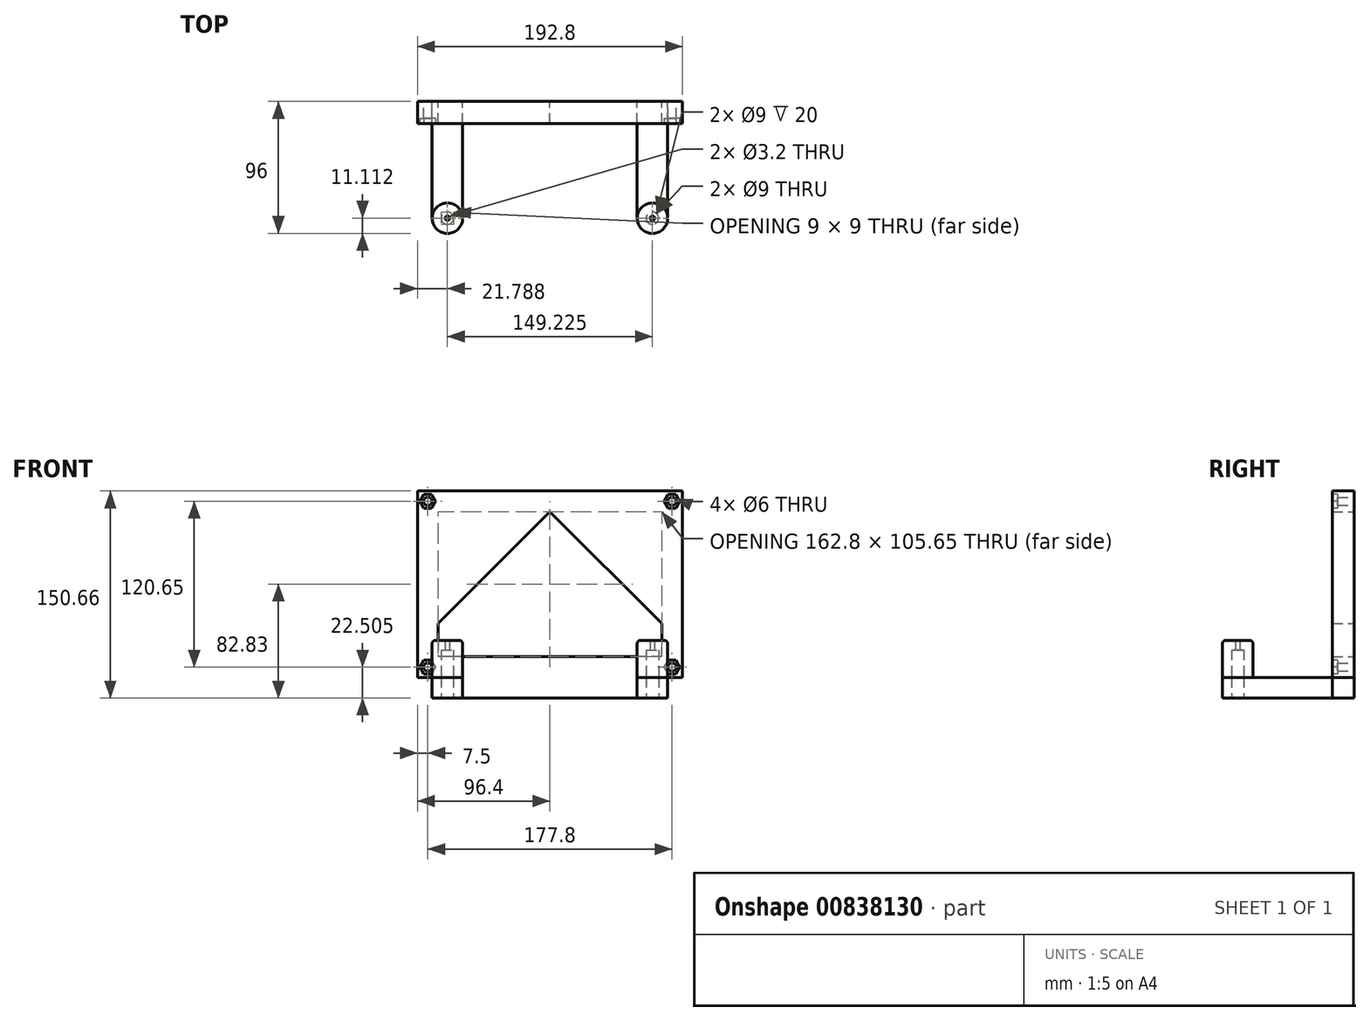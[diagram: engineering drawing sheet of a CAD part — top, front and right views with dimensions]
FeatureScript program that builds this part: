
annotation { "Feature Type Name" : "Feature", "Feature Type Description" : "" }
export const myFeature = defineFeature(function(context is Context, id is Id, definition is map)
    precondition{}
    {
        {
            var Q0;
            Q0=qCreatedBy(makeId("Front.planeOp"),FACE);
            var sketch = newSketch(context, id + "F0", { "sketchPlane" : qUnion([Q0])});
            skLineSegment(sketch, "E0.bottom", {"start": v(-88.9, 60.33) * mm, "end": v(88.9, 60.33) * mm, "construction": true});
            skLineSegment(sketch, "E0.top", {"start": v(-88.9, -60.32) * mm, "end": v(88.9, -60.32) * mm, "construction": true});
            skLineSegment(sketch, "E0.left", {"start": v(-88.9, 60.33) * mm, "end": v(-88.9, -60.32) * mm, "construction": true});
            skLineSegment(sketch, "E0.right", {"start": v(88.9, 60.33) * mm, "end": v(88.9, -60.32) * mm, "construction": true});
            skPoint(sketch, "E0.middle", {"position": v(0, 0) * mm});
            skCircle(sketch, "E1", {"center": v(-88.9, 60.33) * mm, "radius": 3 * mm});
            skCircle(sketch, "E2", {"center": v(88.9, 60.33) * mm, "radius": 3 * mm});
            skCircle(sketch, "E3", {"center": v(88.9, -60.32) * mm, "radius": 3 * mm});
            skCircle(sketch, "E4", {"center": v(-88.9, -60.32) * mm, "radius": 3 * mm});
            skLineSegment(sketch, "E5.bottom", {"start": v(-88.9, 60.33) * mm, "end": v(-96.4, 60.33) * mm, "construction": true});
            skLineSegment(sketch, "E5.top", {"start": v(-88.9, 67.83) * mm, "end": v(-96.4, 67.83) * mm, "construction": true});
            skLineSegment(sketch, "E5.left", {"start": v(-88.9, 60.33) * mm, "end": v(-88.9, 67.83) * mm, "construction": true});
            skLineSegment(sketch, "E5.right", {"start": v(-96.4, 60.33) * mm, "end": v(-96.4, 67.83) * mm, "construction": true});
            skLineSegment(sketch, "E6.bottom", {"start": v(88.9, -60.32) * mm, "end": v(96.4, -60.32) * mm, "construction": true});
            skLineSegment(sketch, "E6.top", {"start": v(88.9, -67.83) * mm, "end": v(96.4, -67.83) * mm, "construction": true});
            skLineSegment(sketch, "E6.left", {"start": v(88.9, -60.32) * mm, "end": v(88.9, -67.83) * mm, "construction": true});
            skLineSegment(sketch, "E6.right", {"start": v(96.4, -60.32) * mm, "end": v(96.4, -67.83) * mm, "construction": true});
            skLineSegment(sketch, "E7.bottom", {"start": v(-96.4, 67.83) * mm, "end": v(-81.4, 67.83) * mm});
            skLineSegment(sketch, "E7.top", {"start": v(-96.4, -67.83) * mm, "end": v(-81.4, -67.83) * mm});
            skLineSegment(sketch, "E7.left", {"start": v(-96.4, 67.83) * mm, "end": v(-96.4, -67.83) * mm});
            skLineSegment(sketch, "E7.right", {"start": v(-81.4, 67.83) * mm, "end": v(-81.4, -67.83) * mm});
            skLineSegment(sketch, "E8.bottom", {"start": v(96.4, -67.83) * mm, "end": v(-96.4, -67.83) * mm});
            skLineSegment(sketch, "E8.top", {"start": v(96.4, -52.82) * mm, "end": v(-96.4, -52.83) * mm});
            skLineSegment(sketch, "E8.left", {"start": v(96.4, -67.83) * mm, "end": v(96.4, -52.82) * mm});
            skLineSegment(sketch, "E8.right", {"start": v(-96.4, -67.83) * mm, "end": v(-96.4, -52.83) * mm});
            skLineSegment(sketch, "E9.bottom", {"start": v(96.4, -67.83) * mm, "end": v(81.4, -67.83) * mm});
            skLineSegment(sketch, "E9.top", {"start": v(96.4, 67.83) * mm, "end": v(81.4, 67.83) * mm});
            skLineSegment(sketch, "E9.left", {"start": v(96.4, -67.83) * mm, "end": v(96.4, 67.83) * mm});
            skLineSegment(sketch, "E9.right", {"start": v(81.4, -67.83) * mm, "end": v(81.4, 67.83) * mm});
            skLineSegment(sketch, "E10.bottom", {"start": v(-96.4, 67.83) * mm, "end": v(96.4, 67.83) * mm});
            skLineSegment(sketch, "E10.top", {"start": v(-96.4, 52.83) * mm, "end": v(96.4, 52.83) * mm});
            skLineSegment(sketch, "E10.left", {"start": v(-96.4, 67.83) * mm, "end": v(-96.4, 52.83) * mm});
            skLineSegment(sketch, "E10.right", {"start": v(96.4, 67.83) * mm, "end": v(96.4, 52.83) * mm});
            skLineSegment(sketch, "E11.bottom", {"start": v(0, -67.83) * mm, "end": v(-85.72, -67.83) * mm, "construction": true});
            skLineSegment(sketch, "E11.top", {"start": v(0, -82.83) * mm, "end": v(-85.72, -82.83) * mm, "construction": true});
            skLineSegment(sketch, "E11.left", {"start": v(0, -67.83) * mm, "end": v(0, -82.83) * mm, "construction": true});
            skLineSegment(sketch, "E11.right", {"start": v(-85.72, -67.83) * mm, "end": v(-85.72, -82.83) * mm, "construction": true});
            skLineSegment(sketch, "E12.bottom", {"start": v(0, -67.83) * mm, "end": v(85.73, -67.83) * mm, "construction": true});
            skLineSegment(sketch, "E12.top", {"start": v(0, -82.83) * mm, "end": v(85.73, -82.83) * mm, "construction": true});
            skLineSegment(sketch, "E12.right", {"start": v(85.73, -67.83) * mm, "end": v(85.73, -82.83) * mm, "construction": true});
            skLineSegment(sketch, "E13.bottom", {"start": v(-85.72, -82.83) * mm, "end": v(85.73, -82.83) * mm});
            skLineSegment(sketch, "E13.top", {"start": v(-85.72, -67.83) * mm, "end": v(85.73, -67.83) * mm});
            skLineSegment(sketch, "E13.left", {"start": v(-85.72, -82.83) * mm, "end": v(-85.72, -67.83) * mm});
            skLineSegment(sketch, "E13.right", {"start": v(85.73, -82.83) * mm, "end": v(85.73, -67.83) * mm});
            skLineSegment(sketch, "E14.bottom", {"start": v(85.73, -67.83) * mm, "end": v(70.73, -67.83) * mm});
            skLineSegment(sketch, "E14.left", {"start": v(85.73, -67.83) * mm, "end": v(85.73, -82.83) * mm});
            skLineSegment(sketch, "E15.bottom", {"start": v(-85.72, -67.83) * mm, "end": v(-63.5, -67.83) * mm});
            skLineSegment(sketch, "E15.top", {"start": v(-85.72, -82.83) * mm, "end": v(-63.5, -82.83) * mm});
            skLineSegment(sketch, "E15.left", {"start": v(-85.72, -67.83) * mm, "end": v(-85.72, -82.83) * mm});
            skLineSegment(sketch, "E15.right", {"start": v(-63.5, -67.83) * mm, "end": v(-63.5, -82.83) * mm});
            skLineSegment(sketch, "E16.bottom", {"start": v(85.73, -67.83) * mm, "end": v(63.5, -67.83) * mm});
            skLineSegment(sketch, "E16.top", {"start": v(85.73, -82.83) * mm, "end": v(63.5, -82.83) * mm});
            skLineSegment(sketch, "E16.right", {"start": v(63.5, -67.83) * mm, "end": v(63.5, -82.83) * mm});
            skLineSegment(sketch, "E17", {"start": v(0, 52.83) * mm, "end": v(81.4, -28.57) * mm});
            skLineSegment(sketch, "E18", {"start": v(0, 52.83) * mm, "end": v(-81.4, -28.57) * mm});
            skCircle(sketch, "E19.cCircle", {"center": v(88.9, 60.33) * mm, "radius": 4.95 * mm, "construction": true});
            skLineSegment(sketch, "E19.0", {"start": v(91.76, 55.38) * mm, "end": v(86.04, 55.38) * mm});
            skLineSegment(sketch, "E19.1", {"start": v(86.04, 55.38) * mm, "end": v(83.18, 60.32) * mm});
            skLineSegment(sketch, "E19.2", {"start": v(83.18, 60.32) * mm, "end": v(86.04, 65.28) * mm});
            skLineSegment(sketch, "E19.3", {"start": v(86.04, 65.27) * mm, "end": v(91.76, 65.27) * mm});
            skLineSegment(sketch, "E19.4", {"start": v(91.76, 65.28) * mm, "end": v(94.62, 60.33) * mm});
            skLineSegment(sketch, "E19.5", {"start": v(94.62, 60.33) * mm, "end": v(91.76, 55.38) * mm});
            skPoint(sketch, "E19.0.midPoint", {"position": v(88.9, 55.38) * mm});
            skCircle(sketch, "E20.cCircle", {"center": v(88.9, -60.32) * mm, "radius": 4.95 * mm, "construction": true});
            skLineSegment(sketch, "E20.0", {"start": v(86.04, -55.37) * mm, "end": v(91.76, -55.37) * mm});
            skLineSegment(sketch, "E20.1", {"start": v(91.76, -55.37) * mm, "end": v(94.62, -60.32) * mm});
            skLineSegment(sketch, "E20.2", {"start": v(94.62, -60.32) * mm, "end": v(91.76, -65.28) * mm});
            skLineSegment(sketch, "E20.3", {"start": v(91.76, -65.28) * mm, "end": v(86.04, -65.28) * mm});
            skLineSegment(sketch, "E20.4", {"start": v(86.04, -65.28) * mm, "end": v(83.18, -60.32) * mm});
            skLineSegment(sketch, "E20.5", {"start": v(83.18, -60.32) * mm, "end": v(86.04, -55.37) * mm});
            skPoint(sketch, "E20.0.midPoint", {"position": v(88.9, -55.37) * mm});
            skCircle(sketch, "E21.cCircle", {"center": v(-88.9, -60.32) * mm, "radius": 4.95 * mm, "construction": true});
            skLineSegment(sketch, "E21.0", {"start": v(-91.76, -55.38) * mm, "end": v(-86.04, -55.38) * mm});
            skLineSegment(sketch, "E21.1", {"start": v(-86.04, -55.38) * mm, "end": v(-83.18, -60.33) * mm});
            skLineSegment(sketch, "E21.2", {"start": v(-83.18, -60.33) * mm, "end": v(-86.04, -65.28) * mm});
            skLineSegment(sketch, "E21.3", {"start": v(-86.04, -65.27) * mm, "end": v(-91.76, -65.27) * mm});
            skLineSegment(sketch, "E21.4", {"start": v(-91.76, -65.28) * mm, "end": v(-94.62, -60.33) * mm});
            skLineSegment(sketch, "E21.5", {"start": v(-94.62, -60.33) * mm, "end": v(-91.76, -55.38) * mm});
            skPoint(sketch, "E21.0.midPoint", {"position": v(-88.9, -55.38) * mm});
            skCircle(sketch, "E22.cCircle", {"center": v(-88.9, 60.33) * mm, "radius": 4.95 * mm, "construction": true});
            skLineSegment(sketch, "E22.0", {"start": v(-86.04, 55.38) * mm, "end": v(-91.76, 55.38) * mm});
            skLineSegment(sketch, "E22.1", {"start": v(-91.76, 55.37) * mm, "end": v(-94.62, 60.33) * mm});
            skLineSegment(sketch, "E22.2", {"start": v(-94.62, 60.32) * mm, "end": v(-91.76, 65.28) * mm});
            skLineSegment(sketch, "E22.3", {"start": v(-91.76, 65.28) * mm, "end": v(-86.04, 65.28) * mm});
            skLineSegment(sketch, "E22.4", {"start": v(-86.04, 65.28) * mm, "end": v(-83.18, 60.33) * mm});
            skLineSegment(sketch, "E22.5", {"start": v(-83.18, 60.33) * mm, "end": v(-86.04, 55.38) * mm});
            skPoint(sketch, "E22.0.midPoint", {"position": v(-88.9, 55.38) * mm});
            skSolve(sketch);
        }
        {
            var Q0;
            Q0=makeQuery(id+"F0.imprint","IMPRINT",FACE,{"disambiguationData":[TD([[makeQuery(id+"F0.imprint","IMPRINT",EDGE,{"derivedFrom":sQuery(id+"F0.wireOp",EDGE,"E1")}),-1.0]])]});
            var Q1;
            Q1=makeQuery(id+"F0.imprint","IMPRINT",FACE,{"disambiguationData":[TD([[makeQuery(id+"F0.imprint","IMPRINT",EDGE,{"derivedFrom":sQuery(id+"F0.wireOp",EDGE,"E2")}),-1.0]])]});
            var Q2;
            {var subQ1=sQuery(id+"F0.wireOp",EDGE,"E7.left");var subQ5=sQuery(id+"F0.wireOp",EDGE,"E10.top");var subQ8=makeQuery(id+"F0.imprint","INTERSECT",VERTEX,{"derivedFrom":[subQ1,subQ5]});Q2=makeQuery(id+"F0.imprint","IMPRINT",FACE,{"disambiguationData":[TD([[makeQuery(id+"F0.imprint","IMPRINT",EDGE,{"disambiguationData":[TD([[subQ8,-1.0]])],"derivedFrom":subQ1}),1.0]])]});}
            var Q3;
            {var subQ0=sQuery(id+"F0.wireOp",EDGE,"E9.right");var subQ3=makeQuery(id+"F0.imprint","INTERSECT",VERTEX,{"derivedFrom":[subQ0,sQuery(id+"F0.wireOp",EDGE,"E17")]});Q3=makeQuery(id+"F0.imprint","IMPRINT",FACE,{"disambiguationData":[TD([[makeQuery(id+"F0.imprint","IMPRINT",EDGE,{"disambiguationData":[TD([[subQ3,-1.0]])],"derivedFrom":subQ0}),-1.0]])]});}
            var Q4;
            {var subQ4=sQuery(id+"F0.wireOp",EDGE,"E10.bottom");Q4=makeQuery(id+"F0.imprint","IMPRINT",FACE,{"disambiguationData":[TD([[makeQuery(id+"F0.imprint","IMPRINT",EDGE,{"derivedFrom":subQ4}),-1.0]])]});}
            var Q5;
            {var subQ2=sQuery(id+"F0.wireOp",EDGE,"E15.right");Q5=makeQuery(id+"F0.imprint","IMPRINT",FACE,{"disambiguationData":[TD([[makeQuery(id+"F0.imprint","IMPRINT",EDGE,{"derivedFrom":subQ2}),1.0]])]});}
            var Q6;
            {var subQ0=sQuery(id+"F0.wireOp",EDGE,"E13.left");Q6=makeQuery(id+"F0.imprint","IMPRINT",FACE,{"disambiguationData":[TD([[makeQuery(id+"F0.imprint","IMPRINT",EDGE,{"derivedFrom":subQ0}),-1.0]])]});}
            var Q7;
            {var subQ2=sQuery(id+"F0.wireOp",EDGE,"E13.right");Q7=makeQuery(id+"F0.imprint","IMPRINT",FACE,{"disambiguationData":[TD([[makeQuery(id+"F0.imprint","IMPRINT",EDGE,{"derivedFrom":subQ2}),1.0]])]});}
            var Q8;
            Q8=makeQuery(id+"F0.imprint","IMPRINT",FACE,{"disambiguationData":[TD([[makeQuery(id+"F0.imprint","IMPRINT",EDGE,{"derivedFrom":sQuery(id+"F0.wireOp",EDGE,"E3")}),-1.0]])]});
            var Q9;
            Q9=makeQuery(id+"F0.imprint","IMPRINT",FACE,{"disambiguationData":[TD([[makeQuery(id+"F0.imprint","IMPRINT",EDGE,{"derivedFrom":sQuery(id+"F0.wireOp",EDGE,"E4")}),-1.0]])]});
            var Q10;
            {var subQ1=sQuery(id+"F0.wireOp",EDGE,"E8.bottom");var subQ3=makeQuery(id+"F0.imprint","IMPRINT",VERTEX,{"derivedFrom":subQ1});Q10=makeQuery(id+"F0.imprint","IMPRINT",FACE,{"disambiguationData":[TD([[makeQuery(id+"F0.imprint","IMPRINT",EDGE,{"disambiguationData":[TD([[subQ3,1.0]])],"derivedFrom":subQ1}),-1.0]])]});}
            var Q11;
            {var subQ0=sQuery(id+"F0.wireOp",EDGE,"E17");Q11=makeQuery(id+"F0.imprint","IMPRINT",FACE,{"disambiguationData":[TD([[makeQuery(id+"F0.imprint","IMPRINT",EDGE,{"derivedFrom":subQ0}),1.0]])]});}
            var Q12;
            {var subQ3=sQuery(id+"F0.wireOp",EDGE,"E18");Q12=makeQuery(id+"F0.imprint","IMPRINT",FACE,{"disambiguationData":[TD([[makeQuery(id+"F0.imprint","IMPRINT",EDGE,{"derivedFrom":subQ3}),-1.0]])]});}
            var Q13;
            {var subQ1=sQuery(id+"F0.wireOp",EDGE,"E7.bottom");Q13=makeQuery(id+"F0.imprint","IMPRINT",FACE,{"disambiguationData":[TD([[makeQuery(id+"F0.imprint","IMPRINT",EDGE,{"derivedFrom":subQ1}),-1.0]])]});}
            var Q14;
            Q14=makeQuery(id+"F0.imprint","IMPRINT",FACE,{"disambiguationData":[TD([[makeQuery(id+"F0.imprint","IMPRINT",EDGE,{"derivedFrom":sQuery(id+"F0.wireOp",EDGE,"E21.0")}),1.0]])]});
            var Q15;
            {var subQ5=sQuery(id+"F0.wireOp",EDGE,"E8.left");Q15=makeQuery(id+"F0.imprint","IMPRINT",FACE,{"disambiguationData":[TD([[makeQuery(id+"F0.imprint","IMPRINT",EDGE,{"derivedFrom":subQ5}),1.0]])]});}
            var Q16;
            {var subQ5=sQuery(id+"F0.wireOp",EDGE,"E9.top");Q16=makeQuery(id+"F0.imprint","IMPRINT",FACE,{"disambiguationData":[TD([[makeQuery(id+"F0.imprint","IMPRINT",EDGE,{"derivedFrom":subQ5}),1.0]])]});}
            extrude(context, id + "F1", {"entities" : qUnion([Q0, Q1, Q2, Q3, Q4, Q5, Q6, Q7, Q8, Q9, Q10, Q11, Q12, Q13, Q14, Q15, Q16]), "depth" : 16 * mm, "offsetDistance" : 25 * mm});
        }
        {
            var Q0;
            {var subQ0=sQuery(id+"F0.wireOp",EDGE,"E13.left");Q0=makeQuery(id+"F0.imprint","IMPRINT",FACE,{"disambiguationData":[TD([[makeQuery(id+"F0.imprint","IMPRINT",EDGE,{"derivedFrom":subQ0}),-1.0]])]});}
            var Q1;
            {var subQ2=sQuery(id+"F0.wireOp",EDGE,"E13.right");Q1=makeQuery(id+"F0.imprint","IMPRINT",FACE,{"disambiguationData":[TD([[makeQuery(id+"F0.imprint","IMPRINT",EDGE,{"derivedFrom":subQ2}),1.0]])]});}
            extrude(context, id + "F2", {"entities" : qUnion([Q0, Q1]), "depth" : 96 * mm, "offsetDistance" : 25 * mm});
        }
        {
            var Q0;
            Q0=makeQuery(id+"F2.opExtrude","SWEPT_FACE",FACE,{"disambiguationData":[OSD([sQuery(id+"F0.wireOp",EDGE,"E8.bottom")])]});
            var Q1;
            Q1=makeQuery(id+"F2.opExtrude","SWEPT_FACE",FACE,{"disambiguationData":[OSD([sQuery(id+"F0.wireOp",EDGE,"E7.top"),sQuery(id+"F0.wireOp",EDGE,"E8.bottom")])]});
            cPlane(context, id + "F3", {"entities" : qUnion([Q0, Q1]), "cplaneType" : CPlaneType.MID_PLANE, "offset" : 25 * mm, "width" : 150 * mm, "height" : 150 * mm});
        }
        {
            var Q0;
            Q0=qCreatedBy(id+"F3.planeOp",FACE);
            var sketch = newSketch(context, id + "F4", { "sketchPlane" : qUnion([Q0])});
            skLineSegment(sketch, "E23.bottom", {"start": v(-85.72, -96) * mm, "end": v(-63.5, -96) * mm, "construction": true});
            skLineSegment(sketch, "E23.top", {"start": v(-85.72, -73.78) * mm, "end": v(-63.5, -73.78) * mm, "construction": true});
            skLineSegment(sketch, "E23.left", {"start": v(-85.72, -96) * mm, "end": v(-85.72, -73.78) * mm, "construction": true});
            skLineSegment(sketch, "E23.right", {"start": v(-63.5, -96) * mm, "end": v(-63.5, -73.78) * mm, "construction": true});
            skLineSegment(sketch, "E24.bottom", {"start": v(63.5, -96) * mm, "end": v(85.73, -96) * mm, "construction": true});
            skLineSegment(sketch, "E24.top", {"start": v(63.5, -73.78) * mm, "end": v(85.73, -73.78) * mm, "construction": true});
            skLineSegment(sketch, "E24.left", {"start": v(63.5, -96) * mm, "end": v(63.5, -73.78) * mm, "construction": true});
            skLineSegment(sketch, "E24.right", {"start": v(85.73, -96) * mm, "end": v(85.73, -73.78) * mm, "construction": true});
            skLineSegment(sketch, "E25", {"start": v(-74.61, -96) * mm, "end": v(-74.61, -84.89) * mm, "construction": true});
            skPoint(sketch, "E25.endSnap0", {"position": v(-63.5, -84.89) * mm});
            skLineSegment(sketch, "E26", {"start": v(74.61, -96) * mm, "end": v(74.61, -84.89) * mm, "construction": true});
            skPoint(sketch, "E26.endSnap0", {"position": v(85.73, -84.89) * mm});
            skCircle(sketch, "E27", {"center": v(-74.61, -84.89) * mm, "radius": 11.11 * mm});
            skCircle(sketch, "E28", {"center": v(74.61, -84.89) * mm, "radius": 11.11 * mm});
            skSolve(sketch);
        }
        {
            var Q0;
            Q0 = qSketchRegion(id + "F4", true);
            extrude(context, id + "F5", {"entities" : qUnion([Q0]), "depth" : 27 * mm, "offsetDistance" : 25 * mm});
        }
        {
            var Q0;
            Q0=makeQuery(id+"F2.opExtrude","CAP_EDGE",EDGE,{"disambiguationData":[OSD([sQuery(id+"F0.wireOp",EDGE,"E16.right")])],"isStart":false});
            var Q1;
            Q1=makeQuery(id+"F2.opExtrude","CAP_EDGE",EDGE,{"disambiguationData":[OSD([sQuery(id+"F0.wireOp",EDGE,"E13.right")])],"isStart":false});
            var Q2;
            Q2=makeQuery(id+"F2.opExtrude","CAP_EDGE",EDGE,{"disambiguationData":[OSD([sQuery(id+"F0.wireOp",EDGE,"E15.right")])],"isStart":false});
            var Q3;
            Q3=makeQuery(id+"F2.opExtrude","CAP_EDGE",EDGE,{"disambiguationData":[OSD([sQuery(id+"F0.wireOp",EDGE,"E13.left")])],"isStart":false});
            fillet(context, id + "F6", {"entities" : qUnion([Q0, Q1, Q2, Q3]), "radius" : 11.1 * mm, "tangentPropagation" : true, "allowEdgeOverflow" : false});
        }
        {
            var Q0;
            Q0=makeQuery(id+"F1.opExtrude","CAP_FACE",FACE,{"disambiguationData":[OSD([sQuery(id+"F0.wireOp",EDGE,"E1"),sQuery(id+"F0.wireOp",EDGE,"E2"),sQuery(id+"F0.wireOp",EDGE,"E3"),sQuery(id+"F0.wireOp",EDGE,"E4"),sQuery(id+"F0.wireOp",EDGE,"E7.bottom"),sQuery(id+"F0.wireOp",EDGE,"E7.top"),sQuery(id+"F0.wireOp",EDGE,"E7.left"),sQuery(id+"F0.wireOp",EDGE,"E7.right"),sQuery(id+"F0.wireOp",EDGE,"E8.bottom"),sQuery(id+"F0.wireOp",EDGE,"E8.top"),sQuery(id+"F0.wireOp",EDGE,"E8.left"),sQuery(id+"F0.wireOp",EDGE,"E9.top"),sQuery(id+"F0.wireOp",EDGE,"E9.left"),sQuery(id+"F0.wireOp",EDGE,"E9.right"),sQuery(id+"F0.wireOp",EDGE,"E10.bottom"),sQuery(id+"F0.wireOp",EDGE,"E13.bottom"),sQuery(id+"F0.wireOp",EDGE,"E13.left"),sQuery(id+"F0.wireOp",EDGE,"E13.right"),sQuery(id+"F0.wireOp",EDGE,"E17"),sQuery(id+"F0.wireOp",EDGE,"E18")])],"isStart":false});
            cPlane(context, id + "F7", {"entities" : qUnion([Q0]), "cplaneType" : CPlaneType.OFFSET, "offset" : 0 * mm, "width" : 150 * mm, "height" : 150 * mm});
        }
        {
            var Q0;
            Q0=qCreatedBy(id+"F7.planeOp",FACE);
            var sketch = newSketch(context, id + "F8", { "sketchPlane" : qUnion([Q0])});
            skCircle(sketch, "E29.cCircle", {"center": v(88.9, 60.33) * mm, "radius": 4.95 * mm, "construction": true});
            skLineSegment(sketch, "E29.0", {"start": v(91.76, 55.38) * mm, "end": v(86.04, 55.38) * mm});
            skLineSegment(sketch, "E29.1", {"start": v(86.04, 55.37) * mm, "end": v(83.18, 60.32) * mm});
            skLineSegment(sketch, "E29.2", {"start": v(83.18, 60.32) * mm, "end": v(86.04, 65.28) * mm});
            skLineSegment(sketch, "E29.3", {"start": v(86.04, 65.28) * mm, "end": v(91.76, 65.28) * mm});
            skLineSegment(sketch, "E29.4", {"start": v(91.76, 65.28) * mm, "end": v(94.62, 60.32) * mm});
            skLineSegment(sketch, "E29.5", {"start": v(94.62, 60.33) * mm, "end": v(91.76, 55.38) * mm});
            skPoint(sketch, "E29.0.midPoint", {"position": v(88.9, 55.38) * mm});
            skCircle(sketch, "E30.cCircle", {"center": v(-88.9, 60.33) * mm, "radius": 4.95 * mm, "construction": true});
            skLineSegment(sketch, "E30.0", {"start": v(-86.04, 55.38) * mm, "end": v(-91.76, 55.38) * mm});
            skLineSegment(sketch, "E30.1", {"start": v(-91.76, 55.38) * mm, "end": v(-94.62, 60.33) * mm});
            skLineSegment(sketch, "E30.2", {"start": v(-94.62, 60.33) * mm, "end": v(-91.76, 65.28) * mm});
            skLineSegment(sketch, "E30.3", {"start": v(-91.76, 65.28) * mm, "end": v(-86.04, 65.28) * mm});
            skLineSegment(sketch, "E30.4", {"start": v(-86.04, 65.28) * mm, "end": v(-83.18, 60.32) * mm});
            skLineSegment(sketch, "E30.5", {"start": v(-83.18, 60.33) * mm, "end": v(-86.04, 55.37) * mm});
            skPoint(sketch, "E30.0.midPoint", {"position": v(-88.9, 55.38) * mm});
            skCircle(sketch, "E31.cCircle", {"center": v(-88.9, -60.32) * mm, "radius": 4.95 * mm, "construction": true});
            skLineSegment(sketch, "E31.0", {"start": v(-86.04, -65.27) * mm, "end": v(-91.76, -65.27) * mm});
            skLineSegment(sketch, "E31.1", {"start": v(-91.76, -65.27) * mm, "end": v(-94.62, -60.32) * mm});
            skLineSegment(sketch, "E31.2", {"start": v(-94.62, -60.32) * mm, "end": v(-91.76, -55.38) * mm});
            skLineSegment(sketch, "E31.3", {"start": v(-91.76, -55.38) * mm, "end": v(-86.04, -55.38) * mm});
            skLineSegment(sketch, "E31.4", {"start": v(-86.04, -55.37) * mm, "end": v(-83.18, -60.32) * mm});
            skLineSegment(sketch, "E31.5", {"start": v(-83.18, -60.32) * mm, "end": v(-86.04, -65.27) * mm});
            skPoint(sketch, "E31.0.midPoint", {"position": v(-88.9, -65.28) * mm});
            skCircle(sketch, "E32.cCircle", {"center": v(88.9, -60.32) * mm, "radius": 4.95 * mm, "construction": true});
            skLineSegment(sketch, "E32.0", {"start": v(91.76, -65.28) * mm, "end": v(86.04, -65.28) * mm});
            skLineSegment(sketch, "E32.1", {"start": v(86.04, -65.28) * mm, "end": v(83.18, -60.32) * mm});
            skLineSegment(sketch, "E32.2", {"start": v(83.18, -60.32) * mm, "end": v(86.04, -55.37) * mm});
            skLineSegment(sketch, "E32.3", {"start": v(86.04, -55.37) * mm, "end": v(91.76, -55.37) * mm});
            skLineSegment(sketch, "E32.4", {"start": v(91.76, -55.38) * mm, "end": v(94.62, -60.32) * mm});
            skLineSegment(sketch, "E32.5", {"start": v(94.62, -60.33) * mm, "end": v(91.76, -65.28) * mm});
            skPoint(sketch, "E32.0.midPoint", {"position": v(88.9, -65.28) * mm});
            skSolve(sketch);
        }
        {
            var Q0;
            Q0 = qSketchRegion(id + "F8", true);
            extrude(context, id + "F9", {"entities" : qUnion([Q0]), "operationType" : NewBodyOperationType.REMOVE, "oppositeDirection" : true, "depth" : 3.8 * mm, "offsetDistance" : 25 * mm});
        }
        {
            var Q0;
            {var subQ0=sQuery(id+"F0.wireOp",EDGE,"E13.bottom");Q0=makeQuery(id+"F2.opExtrude","SWEPT_FACE",FACE,{"disambiguationData":[OSD([subQ0]),TDD([makeQuery(id+"F0.imprint","IMPRINT",EDGE,{"disambiguationData":[TD([[makeQuery(id+"F0.imprint","INTERSECT",VERTEX,{"derivedFrom":[subQ0,sQuery(id+"F0.wireOp",EDGE,"E15.right")]}),1.0]])],"derivedFrom":subQ0})])]});}
            var Q1;
            {var subQ0=sQuery(id+"F0.wireOp",EDGE,"E13.bottom");Q1=makeQuery(id+"F2.opExtrude","SWEPT_FACE",FACE,{"disambiguationData":[OSD([subQ0]),TDD([makeQuery(id+"F0.imprint","IMPRINT",EDGE,{"disambiguationData":[TD([[makeQuery(id+"F0.imprint","INTERSECT",VERTEX,{"derivedFrom":[subQ0,sQuery(id+"F0.wireOp",EDGE,"E13.right")]}),1.0]])],"derivedFrom":subQ0})])]});}
            cPlane(context, id + "F10", {"entities" : qUnion([Q0, Q1]), "cplaneType" : CPlaneType.MID_PLANE, "offset" : 25 * mm, "width" : 150 * mm, "height" : 150 * mm});
        }
        {
            var Q0;
            Q0=qCreatedBy(id+"F10.planeOp",FACE);
            var sketch = newSketch(context, id + "F11", { "sketchPlane" : qUnion([Q0])});
            skPoint(sketch, "E33", {"position": v(74.61, 84.89) * mm});
            skPoint(sketch, "E34", {"position": v(-74.61, 84.89) * mm});
            skSolve(sketch);
        }
        {
            var Q0;
            Q0=sQuery(id+"F11.wireOp",VERTEX,"E34");
            var Q1;
            Q1=sQuery(id+"F11.wireOp",VERTEX,"E33");
            var Q2;
            Q2=makeQuery(id+"F2.opExtrude","SWEPT_BODY",BODY,{"disambiguationData":[OSD([sQuery(id+"F0.wireOp",EDGE,"E8.bottom"),sQuery(id+"F0.wireOp",EDGE,"E13.bottom"),sQuery(id+"F0.wireOp",EDGE,"E13.right"),sQuery(id+"F0.wireOp",EDGE,"E16.right")])]});
            var Q3;
            Q3=makeQuery(id+"F2.opExtrude","SWEPT_BODY",BODY,{"disambiguationData":[OSD([sQuery(id+"F0.wireOp",EDGE,"E7.top"),sQuery(id+"F0.wireOp",EDGE,"E8.bottom"),sQuery(id+"F0.wireOp",EDGE,"E13.bottom"),sQuery(id+"F0.wireOp",EDGE,"E13.left"),sQuery(id+"F0.wireOp",EDGE,"E15.right")])]});
            var Q4;
            Q4=makeQuery(id+"F5.opExtrude","SWEPT_BODY",BODY,{"disambiguationData":[OSD([sQuery(id+"F4.wireOp",EDGE,"E27")])]});
            var Q5;
            Q5=makeQuery(id+"F5.opExtrude","SWEPT_BODY",BODY,{"disambiguationData":[OSD([sQuery(id+"F4.wireOp",EDGE,"E28")])]});
            hole(context, id + "F12", {"style" : HoleStyle.C_BORE, "endStyle" : HoleEndStyle.THROUGH, "holeDiameter" : 3.2 * mm, "cBoreDiameter" : 9 * mm, "cBoreDepth" : 35 * mm, "majorDiameter" : 5 * mm, "isTappedThrough" : true, "tappedDepth" : 12 * mm, "tapClearance" : 3, "locations" : qUnion([Q0, Q1]), "scope" : qUnion([Q2, Q3, Q4, Q5])});
        }
        {
            var Q0;
            Q0=makeQuery(id+"F5.opExtrude","CAP_EDGE",EDGE,{"disambiguationData":[OSD([sQuery(id+"F4.wireOp",EDGE,"E27")])],"isStart":false});
            var Q1;
            Q1=makeQuery(id+"F5.opExtrude","CAP_EDGE",EDGE,{"disambiguationData":[OSD([sQuery(id+"F4.wireOp",EDGE,"E28")])],"isStart":false});
            fillet(context, id + "F13", {"entities" : qUnion([Q0, Q1]), "radius" : 2.5 * mm, "tangentPropagation" : true, "allowEdgeOverflow" : false});
        }
    });
